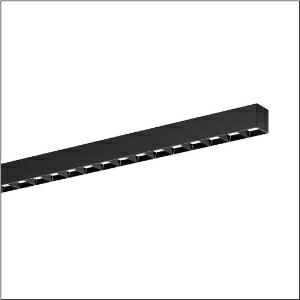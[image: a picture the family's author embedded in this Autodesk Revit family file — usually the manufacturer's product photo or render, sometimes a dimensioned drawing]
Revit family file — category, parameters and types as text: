
# Revit family: silica_21_51mx22dc4abb
name_source: partatom
category: Lighting Fixtures
units: mm (PartAtom-declared; Revit-internal decimal feet)

## family parameters
Cut with Voids When Loaded = No
Host = Face
Light Source = No
Part Type = Normal
Room Calculation Point = No
Round Connector Dimension = Use Diameter
Shared = No

## types (1)
- --- (1 x LED, 10800 lm, 64.7 W, 4000K)
    Apparent Load = 65 VA
    CIE Flux Codes = 86 100 100 100 100
    Color Rendering = 80
    Color Temperature = 4000K
    Default Elevation = 1800 mm
    Description = Silica 21, office luminaire, primary light control with darklight reflector, of PMMA, black, CAT 2 (L<= 3000cd/m²), light emission: direct distribution, primary light characteristic: symmetric, installation type: surface-mounted, LED, rated luminous flux: 10.800lm, luminous efficacy: 167lm/W, light colour: 840, colour temperature: 4000K, control gear: DALI 2, with terminal, 3+2-pole, max. 2.5mm², mains connection: 220..240V, AC, 50/60Hz, rated input power: 64.7W, luminaire housing, of aluminium, matt jet black (RAL 9005), length: 3.004mm, width: 53mm, height: 53mm, protection rating (complete): IP20, insulation class (complete): insulation class I (protective earthing), certification: CE, permissible operating ambient temperature: 0..+35°C, standard: EN 50419, packaging unit: 1 piece
    Height = 53 mm
    Lamp = 1 x LED
    Lamp Light Flux = 10800 lm
    Lamp Power = 64.7 W
    Lamp count = 1
    Length = 3004 mm
    Luminous efficacy = 167 lm/W
    Manufacturer = Siteco
    ModVariant = No
    Model = 51MX22DC4ABB
    Mounting Place = Ceiling
    Mounting Type = Surface mounted
    Number of Poles = 1
    OnlyDefault = Yes
    Power Factor = 1
    Product Name = Silica 21
    Product group = office luminaire | ceiling mounted
    ProductGroupID = 301
    Protection Class = Protection class I
    Protection Degree = IP 20
    RLX_Detail_Level = 1
    RLX_Emergency_Light_Flux = 0 lm
    RLX_Emergency_Type = 0
    RLX_Emergency_Type_DB = No
    RlxData = <blob elided: 65529 chars, md5=13ec0985>
    Socket = socket
    Standby Power = 0 W
    System Light Flux = 10800 lm
    System Power = 65 W
    Type Comments = factory setting: luminous flux: 100 % | dim-lin: 254 | 366 mA
    Type Image = l_1335908.jpg
    URL = http://relux.com
    VarID = @adj_126437
    Voltage = 0 V
    Weight = 0.00 kg
    Width = 53 mm

## geometry (parser evidence)
native form markers: Blend x4, Sweep x11
no freeform markers — native parametric forms only
